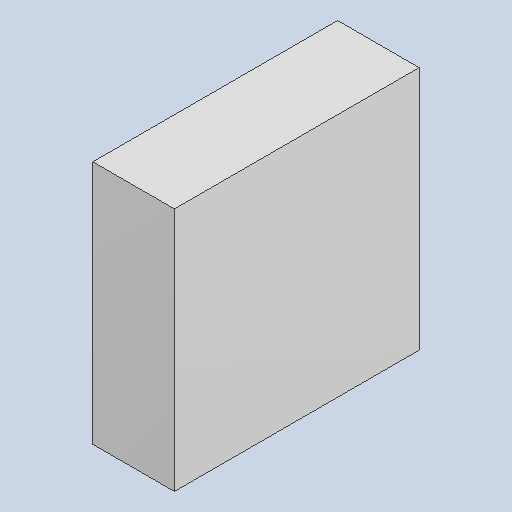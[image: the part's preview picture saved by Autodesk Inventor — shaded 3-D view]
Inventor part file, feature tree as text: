
AUTODESK INVENTOR PART (.ipt)
format: ipt  version: 2023.4 (Build 274418000, 418)  size: 81,408 bytes
history: native  units: mm
features: extrude x1
ambient origin geometry x8: Origin, YZ Plane, XZ Plane, XY Plane, X Axis, Y Axis, Z Axis, Center Point
bodies: Solid1 (feature_tree)
feature tree (1):
  extrude  "Extruded_17"  [1 undecoded]
note: 1 required parameter value undecoded (feature->parameter linkage not recoverable at this tier; creation-order binding heuristic only, values carry confidence <= 0.55)
